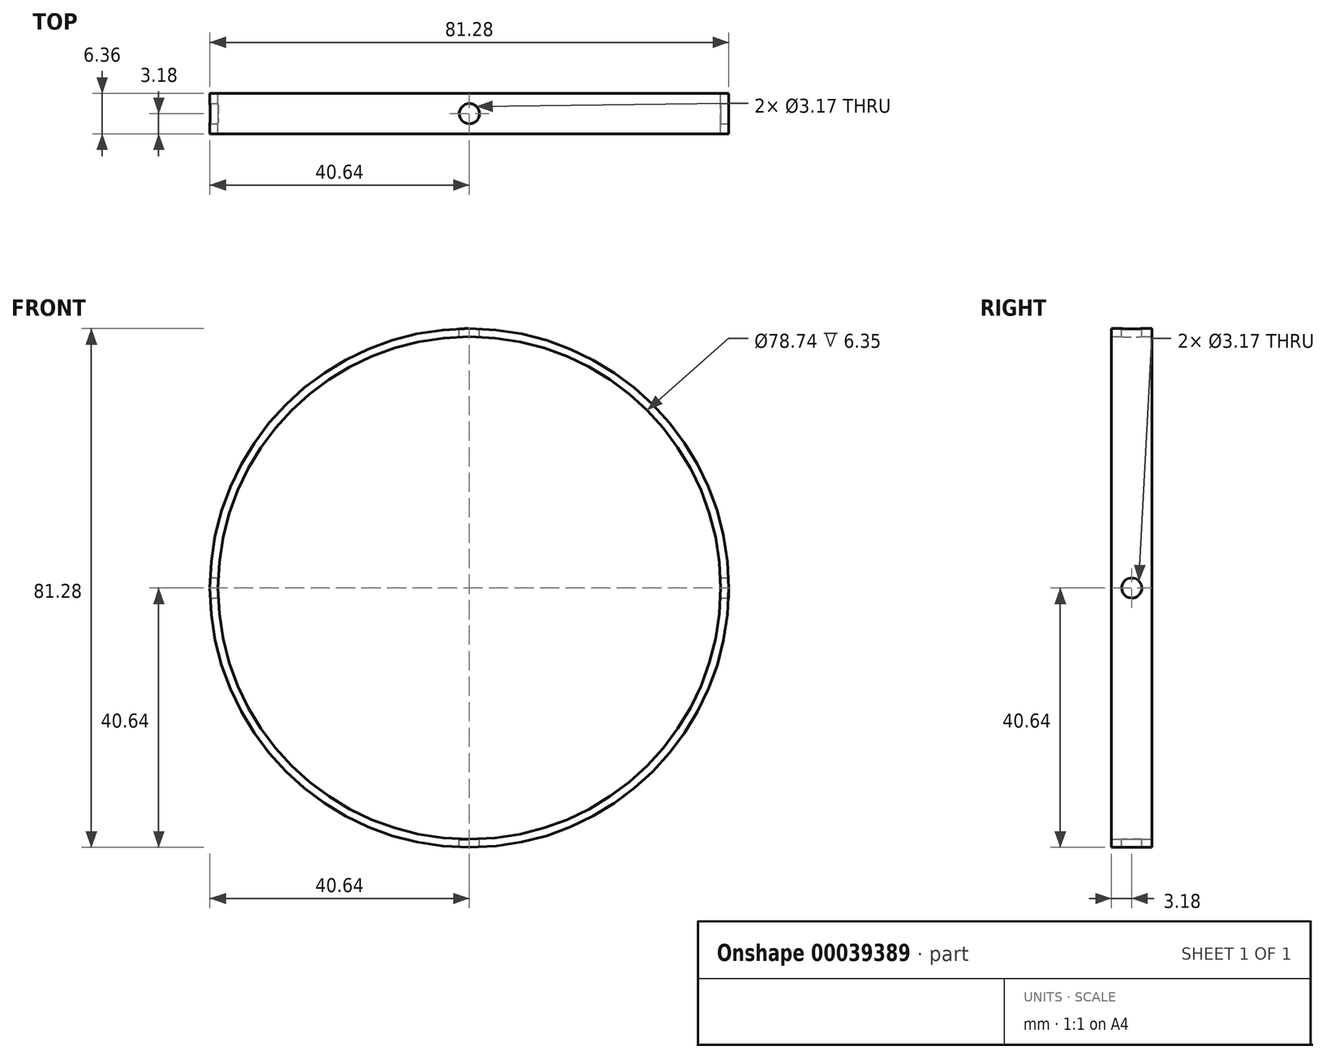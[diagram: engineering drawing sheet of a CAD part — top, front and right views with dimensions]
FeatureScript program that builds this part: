
annotation { "Feature Type Name" : "Feature", "Feature Type Description" : "" }
export const myFeature = defineFeature(function(context is Context, id is Id, definition is map)
    precondition{}
    {
        {
            var Q0;
            Q0=qCreatedBy(makeId("Front.planeOp"),FACE);
            var sketch = newSketch(context, id + "F0", { "sketchPlane" : qUnion([Q0])});
            skCircle(sketch, "E0", {"center": v(0, 0) * mm, "radius": 39.37 * mm});
            skCircle(sketch, "E1", {"center": v(0, 0) * mm, "radius": 40.64 * mm});
            skSolve(sketch);
        }
        {
            var Q0;
            Q0=makeQuery(id+"F0.imprint","IMPRINT",FACE,{"disambiguationData":[TD([[makeQuery(id+"F0.imprint","IMPRINT",EDGE,{"derivedFrom":sQuery(id+"F0.wireOp",EDGE,"E0")}),-1.0]])]});
            extrude(context, id + "F1", {"entities" : qUnion([Q0]), "endBound" : BoundingType.SYMMETRIC, "depth" : 6.35 * mm});
        }
        {
            var Q0;
            Q0=qCreatedBy(makeId("Top.planeOp"),FACE);
            var sketch = newSketch(context, id + "F2", { "sketchPlane" : qUnion([Q0])});
            skCircle(sketch, "E2", {"center": v(0, 0) * mm, "radius": 1.59 * mm});
            skSolve(sketch);
        }
        {
            var Q0;
            Q0=qCreatedBy(makeId("Right.planeOp"),FACE);
            var sketch = newSketch(context, id + "F3", { "sketchPlane" : qUnion([Q0])});
            skCircle(sketch, "E3", {"center": v(0, 0) * mm, "radius": 1.59 * mm});
            skSolve(sketch);
        }
        {
            var Q0;
            Q0=makeQuery(id+"F2.imprint","IMPRINT",FACE,{"disambiguationData":[TD([[makeQuery(id+"F2.imprint","IMPRINT",EDGE,{"derivedFrom":sQuery(id+"F2.wireOp",EDGE,"E2")}),1.0]])]});
            extrude(context, id + "F4", {"entities" : qUnion([Q0]), "operationType" : NewBodyOperationType.REMOVE, "endBound" : BoundingType.THROUGH_ALL, "oppositeDirection" : true, "depth" : 96.52 * mm, "hasSecondDirection" : true, "secondDirectionOppositeDirection" : false, "secondDirectionDepth" : 49.78 * mm});
        }
        {
            var Q0;
            Q0=makeQuery(id+"F3.imprint","IMPRINT",FACE,{"disambiguationData":[TD([[makeQuery(id+"F3.imprint","IMPRINT",EDGE,{"derivedFrom":sQuery(id+"F3.wireOp",EDGE,"E3")}),1.0]])]});
            extrude(context, id + "F5", {"entities" : qUnion([Q0]), "operationType" : NewBodyOperationType.REMOVE, "endBound" : BoundingType.THROUGH_ALL, "oppositeDirection" : true, "depth" : 25.4 * mm, "hasSecondDirection" : true, "secondDirectionOppositeDirection" : false, "secondDirectionDepth" : 44.72 * mm});
        }
    });
